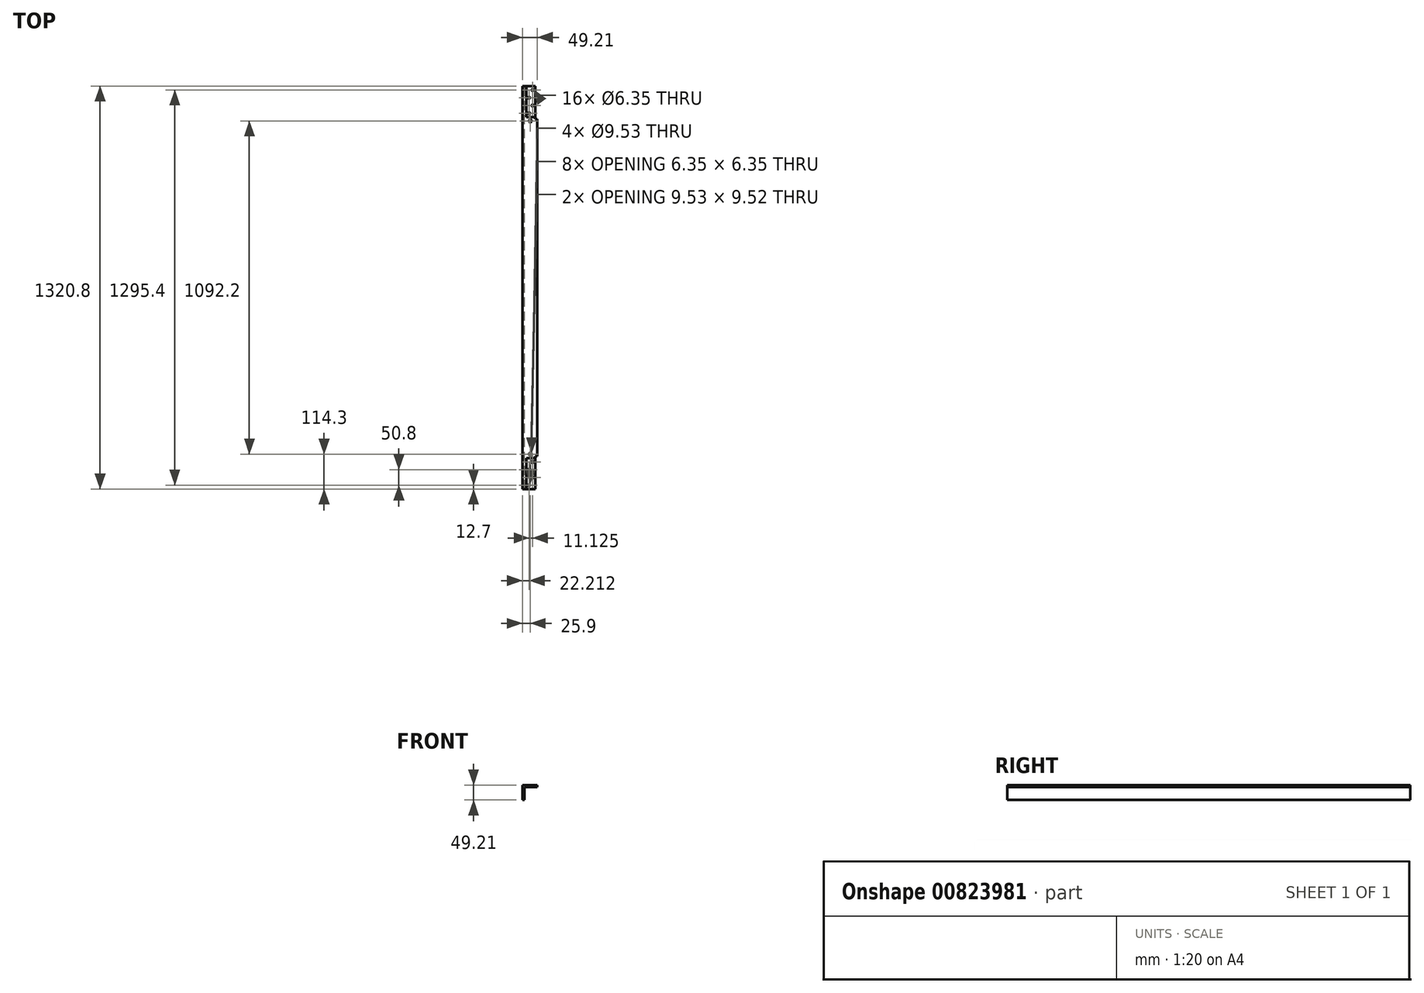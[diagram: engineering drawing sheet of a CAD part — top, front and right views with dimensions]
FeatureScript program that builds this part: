
annotation { "Feature Type Name" : "Feature", "Feature Type Description" : "" }
export const myFeature = defineFeature(function(context is Context, id is Id, definition is map)
    precondition{}
    {
        {
            var Q0;
            Q0=qCreatedBy(makeId("Front.planeOp"),FACE);
            var sketch = newSketch(context, id + "F0", { "sketchPlane" : qUnion([Q0])});
            skLineSegment(sketch, "E0.MirrorCS", {"start": v(-25.9, 26.91) * mm, "end": v(23.31, 26.91) * mm});
            skLineSegment(sketch, "E1.MirrorCS", {"start": v(23.31, 26.91) * mm, "end": v(23.31, 20.56) * mm});
            skLineSegment(sketch, "E2.MirrorCS", {"start": v(23.31, 20.56) * mm, "end": v(-19.55, 20.56) * mm});
            skLineSegment(sketch, "E3.MirrorCS", {"start": v(-19.55, 20.56) * mm, "end": v(-19.55, -22.3) * mm});
            skLineSegment(sketch, "E4.MirrorCS", {"start": v(-25.9, -22.3) * mm, "end": v(-25.9, 26.91) * mm});
            skLineSegment(sketch, "E5.MirrorCS", {"start": v(-25.9, -22.3) * mm, "end": v(-19.55, -22.3) * mm});
            skSolve(sketch);
        }
        {
            var Q0;
            Q0=makeQuery(id+"F0.imprint","IMPRINT",FACE,{"disambiguationData":[TD([[makeQuery(id+"F0.imprint","IMPRINT",EDGE,{"derivedFrom":sQuery(id+"F0.wireOp",EDGE,"E0.MirrorCS")}),-1.0]])]});
            extrude(context, id + "F1", {"entities" : qUnion([Q0]), "endBound" : BoundingType.SYMMETRIC, "depth" : 1320.8 * mm, "offsetDistance" : 25.4 * mm});
        }
        {
            var Q0;
            Q0=makeQuery(id+"F1.opExtrude","SWEPT_FACE",FACE,{"disambiguationData":[OSD([sQuery(id+"F0.wireOp",EDGE,"E0.MirrorCS")])]});
            var sketch = newSketch(context, id + "F2", { "sketchPlane" : qUnion([Q0])});
            skLineSegment(sketch, "E6.left", {"start": v(23.31, 552.55) * mm, "end": v(23.31, 660.4) * mm});
            skLineSegment(sketch, "E6.right", {"start": v(-13.21, 558.8) * mm, "end": v(-13.21, 660.4) * mm});
            skLineSegment(sketch, "E7", {"start": v(-13.21, 558.8) * mm, "end": v(16.96, 558.8) * mm});
            skLineSegment(sketch, "E8", {"start": v(16.96, 558.8) * mm, "end": v(16.96, 660.4) * mm});
            skLineSegment(sketch, "E9", {"start": v(16.96, 660.4) * mm, "end": v(-13.21, 660.4) * mm});
            skCircle(sketch, "E10", {"center": v(-3.69, 571.5) * mm, "radius": 3.18 * mm});
            skCircle(sketch, "E11", {"center": v(-3.69, 622.3) * mm, "radius": 3.18 * mm});
            skCircle(sketch, "E12", {"center": v(7.44, 596.9) * mm, "radius": 3.18 * mm});
            skCircle(sketch, "E13", {"center": v(7.44, 647.7) * mm, "radius": 3.18 * mm});
            skLineSegment(sketch, "E14.top", {"start": v(23.31, -552.55) * mm, "end": v(-13.21, -552.55) * mm});
            skLineSegment(sketch, "E14.right", {"start": v(-13.21, -660.4) * mm, "end": v(-13.21, -552.55) * mm});
            skLineSegment(sketch, "E15", {"start": v(-13.21, -660.4) * mm, "end": v(16.96, -660.4) * mm});
            skLineSegment(sketch, "E16", {"start": v(16.96, -660.4) * mm, "end": v(16.96, -558.8) * mm});
            skLineSegment(sketch, "E17", {"start": v(16.96, -558.8) * mm, "end": v(-13.21, -558.8) * mm});
            skLineSegment(sketch, "E18", {"start": v(16.96, -558.8) * mm, "end": v(16.96, -552.55) * mm});
            skCircle(sketch, "E19", {"center": v(-3.69, -647.7) * mm, "radius": 3.18 * mm});
            skCircle(sketch, "E20", {"center": v(-3.69, -596.9) * mm, "radius": 3.18 * mm});
            skCircle(sketch, "E21", {"center": v(7.44, -622.3) * mm, "radius": 3.18 * mm});
            skCircle(sketch, "E22", {"center": v(7.44, -571.5) * mm, "radius": 3.18 * mm});
            skLineSegment(sketch, "E23", {"start": v(16.96, 660.4) * mm, "end": v(23.31, 660.4) * mm});
            skLineSegment(sketch, "E24", {"start": v(23.31, 552.55) * mm, "end": v(-13.21, 552.55) * mm});
            skLineSegment(sketch, "E25", {"start": v(-13.21, 552.55) * mm, "end": v(-13.21, 558.8) * mm});
            skLineSegment(sketch, "E26", {"start": v(16.96, 558.8) * mm, "end": v(16.96, 552.55) * mm});
            skLineSegment(sketch, "E27", {"start": v(16.96, -660.4) * mm, "end": v(23.31, -660.4) * mm});
            skLineSegment(sketch, "E28", {"start": v(23.31, -660.4) * mm, "end": v(23.31, -552.55) * mm});
            skCircle(sketch, "E29", {"center": v(0, 546.1) * mm, "radius": 4.76 * mm});
            skCircle(sketch, "E30.MirrorC", {"center": v(0, -546.1) * mm, "radius": 4.76 * mm});
            skSolve(sketch);
        }
        {
            var Q0;
            {var subQ1=sQuery(id+"F2.wireOp",EDGE,"E6.left");Q0=makeQuery(id+"F2.imprint","IMPRINT",FACE,{"disambiguationData":[TD([[makeQuery(id+"F2.imprint","IMPRINT",EDGE,{"derivedFrom":subQ1}),1.0]])]});}
            var Q1;
            Q1=makeQuery(id+"F2.imprint","IMPRINT",FACE,{"disambiguationData":[TD([[makeQuery(id+"F2.imprint","IMPRINT",EDGE,{"derivedFrom":sQuery(id+"F2.wireOp",EDGE,"E16")}),-1.0]])]});
            extrude(context, id + "F3", {"entities" : qUnion([Q0, Q1]), "operationType" : NewBodyOperationType.REMOVE, "endBound" : BoundingType.THROUGH_ALL, "oppositeDirection" : true, "depth" : 25.4 * mm, "offsetDistance" : 25.4 * mm});
        }
        {
            var Q0;
            {var subQ1=sQuery(id+"F2.wireOp",EDGE,"E15");Q0=makeQuery(id+"F2.imprint","IMPRINT",FACE,{"disambiguationData":[TD([[makeQuery(id+"F2.imprint","IMPRINT",EDGE,{"derivedFrom":subQ1}),1.0]])]});}
            var Q1;
            Q1=makeQuery(id+"F2.imprint","IMPRINT",FACE,{"disambiguationData":[TD([[makeQuery(id+"F2.imprint","IMPRINT",EDGE,{"derivedFrom":sQuery(id+"F2.wireOp",EDGE,"E6.right")}),-1.0]])]});
            extrude(context, id + "F4", {"entities" : qUnion([Q0, Q1]), "operationType" : NewBodyOperationType.REMOVE, "oppositeDirection" : true, "depth" : 3.17 * mm, "offsetDistance" : 25.4 * mm});
        }
        {
            var Q0;
            Q0=sQuery(id+"F2.wireOp",VERTEX,"E20.center");
            var Q1;
            Q1=sQuery(id+"F2.wireOp",VERTEX,"E22.center");
            var Q2;
            Q2=sQuery(id+"F2.wireOp",VERTEX,"E21.center");
            var Q3;
            Q3=sQuery(id+"F2.wireOp",VERTEX,"E19.center");
            var Q4;
            Q4=sQuery(id+"F2.wireOp",VERTEX,"E12.center");
            var Q5;
            Q5=sQuery(id+"F2.wireOp",VERTEX,"E11.center");
            var Q6;
            Q6=sQuery(id+"F2.wireOp",VERTEX,"E13.center");
            var Q7;
            Q7=sQuery(id+"F2.wireOp",VERTEX,"E10.center");
            var Q8;
            Q8=makeQuery(id+"F1.opExtrude","SWEPT_BODY",BODY,{"disambiguationData":[OSD([sQuery(id+"F0.wireOp",EDGE,"E0.MirrorCS"),sQuery(id+"F0.wireOp",EDGE,"E1.MirrorCS"),sQuery(id+"F0.wireOp",EDGE,"E2.MirrorCS"),sQuery(id+"F0.wireOp",EDGE,"E3.MirrorCS"),sQuery(id+"F0.wireOp",EDGE,"E4.MirrorCS"),sQuery(id+"F0.wireOp",EDGE,"E5.MirrorCS")])]});
            hole(context, id + "F5", {"style" : HoleStyle.SIMPLE, "endStyle" : HoleEndStyle.THROUGH, "holeDiameter" : 6.35 * mm, "majorDiameter" : 6.35 * mm, "isTappedThrough" : true, "tappedDepth" : 12.7 * mm, "tapClearance" : 3, "locations" : qUnion([Q0, Q1, Q2, Q3, Q4, Q5, Q6, Q7]), "scope" : qUnion([Q8])});
        }
        {
            var Q0;
            Q0=sQuery(id+"F2.wireOp",VERTEX,"E30.MirrorC.center");
            var Q1;
            Q1=sQuery(id+"F2.wireOp",VERTEX,"E29.center");
            var Q2;
            Q2=makeQuery(id+"F1.opExtrude","SWEPT_BODY",BODY,{"disambiguationData":[OSD([sQuery(id+"F0.wireOp",EDGE,"E0.MirrorCS"),sQuery(id+"F0.wireOp",EDGE,"E1.MirrorCS"),sQuery(id+"F0.wireOp",EDGE,"E2.MirrorCS"),sQuery(id+"F0.wireOp",EDGE,"E3.MirrorCS"),sQuery(id+"F0.wireOp",EDGE,"E4.MirrorCS"),sQuery(id+"F0.wireOp",EDGE,"E5.MirrorCS")])]});
            hole(context, id + "F6", {"style" : HoleStyle.SIMPLE, "endStyle" : HoleEndStyle.THROUGH, "holeDiameter" : 9.52 * mm, "majorDiameter" : 6.35 * mm, "isTappedThrough" : true, "tappedDepth" : 12.7 * mm, "tapClearance" : 3, "locations" : qUnion([Q0, Q1]), "scope" : qUnion([Q2])});
        }
    });
